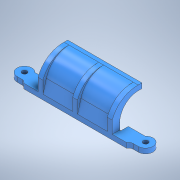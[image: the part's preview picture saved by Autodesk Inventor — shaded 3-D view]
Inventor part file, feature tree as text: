
AUTODESK INVENTOR PART (.ipt)
format: ipt  version: 2022 (Build 260153000, 153)  size: 220,160 bytes
history: native  units: mm
features: sketch x4, extrude x3, mirror x1, plane x1, pattern_linear x1
ambient origin geometry x8: Origin, YZ Plane, XZ Plane, XY Plane, X Axis, Y Axis, Z Axis, Center Point
bodies: Solid1 (feature_tree)
feature tree (10):
  extrude  "Extrusion1"  Depth=6.0mm
  extrude  "Extrusion2"  TaperAngle=0.0deg  [1 undecoded]
  mirror  "Mirror1"
  plane  "Work Plane1"
  extrude  "Extrusion3"  Depth=3.0mm
  pattern_linear  "Rectangular Pattern1"  Spacing1=4.0mm  [1 undecoded]
  sketch  "Sketch5"  dims[d7=4.0mm d8=4.0mm d9=4.0mm d10=2.0mm d11=2.0mm d12=0.0mm d13=2.0mm d14=9.0mm d15=10.0mm d16=12.0mm d17=3.0mm d20=15.0mm d21=2.5mm d22=7.5mm d23=12.0mm d24=2.0mm d25=15.0mm d26=0.0mm d27=2.0mm d28=0.0mm d29=20.0mm d31=14.0mm d32=20.0mm d34=14.0mm]
  sketch  "Sketch1"  dims[d0=24.5mm d1=6.0mm]
  sketch  "Sketch2"  dims[d2=2.0mm d3=0.0mm]
  sketch  "Sketch4"  dims[d4=0.0mm d6=3.0mm]
note: 2 required parameter values undecoded (feature->parameter linkage not recoverable at this tier; creation-order binding heuristic only, values carry confidence <= 0.55)
